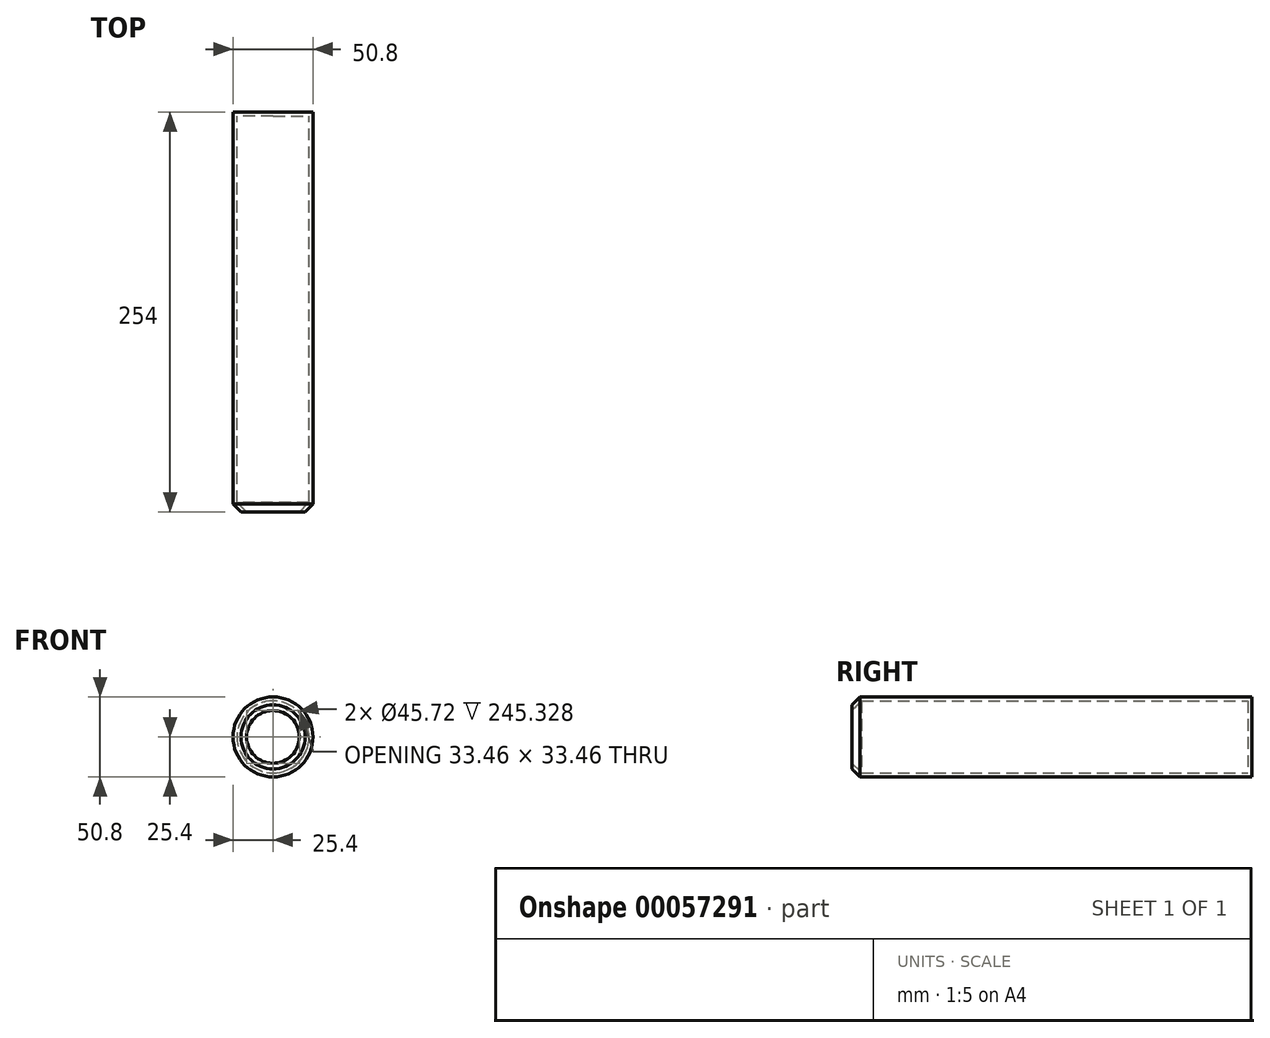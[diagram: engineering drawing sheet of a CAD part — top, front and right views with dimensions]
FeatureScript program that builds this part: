
annotation { "Feature Type Name" : "Feature", "Feature Type Description" : "" }
export const myFeature = defineFeature(function(context is Context, id is Id, definition is map)
    precondition{}
    {
        {
            var Q0;
            Q0=qCreatedBy(makeId("Front.planeOp"),FACE);
            var sketch = newSketch(context, id + "F0", { "sketchPlane" : qUnion([Q0])});
            skCircle(sketch, "E0", {"center": v(0, 0) * mm, "radius": 25.4 * mm});
            skSolve(sketch);
        }
        {
            var Q0;
            Q0=makeQuery(id+"F0.imprint","IMPRINT",FACE,{"disambiguationData":[TD([[makeQuery(id+"F0.imprint","IMPRINT",EDGE,{"derivedFrom":sQuery(id+"F0.wireOp",EDGE,"E0")}),1.0]])]});
            extrude(context, id + "F1", {"entities" : qUnion([Q0]), "depth" : 254 * mm});
        }
        {
            var Q0;
            Q0=makeQuery(id+"F1.opExtrude","CAP_EDGE",EDGE,{"disambiguationData":[OSD([sQuery(id+"F0.wireOp",EDGE,"E0")])],"isStart":false});
            chamfer(context, id + "F2", {"entities" : qUnion([Q0]), "width" : 5.08 * mm, "tangentPropagation" : true});
        }
        {
            var Q0;
            Q0=makeQuery(id+"F1.opExtrude","CAP_FACE",FACE,{"disambiguationData":[OSD([sQuery(id+"F0.wireOp",EDGE,"E0")])],"isStart":false});
            shell(context, id + "F3", {"entities" : qUnion([Q0]), "thickness" : 2.54 * mm});
        }
    });
